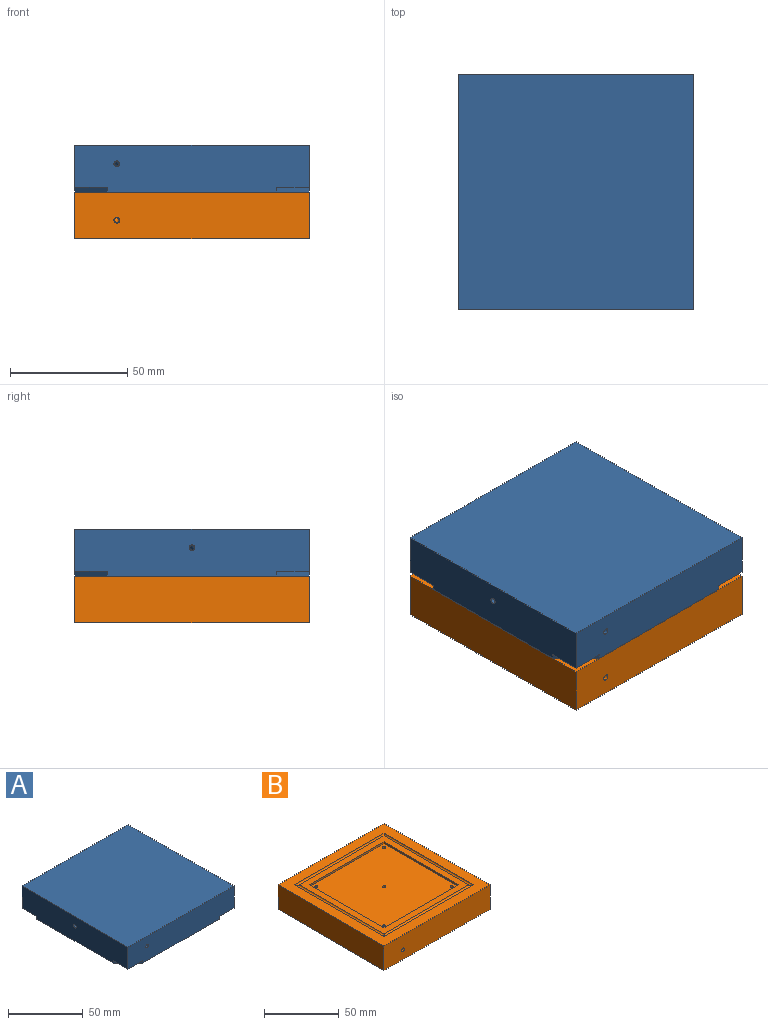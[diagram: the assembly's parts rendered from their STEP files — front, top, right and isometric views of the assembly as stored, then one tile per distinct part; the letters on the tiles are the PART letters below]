
ASSEMBLY  parts=2 mates=1
PART A: 49 faces, bbox 100x100x20 mm
  f0: cylinder r=1mm len=10.75mm, axis (0,1,0), area 67.5mm2, adj f35,f47
  f1: cylinder r=1mm len=8.75mm, axis (1,0,0), area 55mm2, adj f14,f45
  f2: cylinder r=1mm len=10.75mm, axis (0,-1,0), area 67.5mm2, adj f33,f43
  f3: cylinder r=1mm len=41.75mm, axis (-1,0,0), area 262.3mm2, adj f15,f41
  f4: cylinder r=1mm len=10.75mm, axis (-1,0,0), area 67.5mm2, adj f31,f39
  f5: cylinder r=1mm len=10.75mm, axis (-1,0,0), area 67.5mm2, adj f29,f37
  f6: plane 100x100mm, normal (0,0,-1), area 4708mm2, adj f9,f10,f11,f12,f16,f18,f20,f22
  f7: cylinder r=1mm len=5.5mm, axis (0,0,-1), area 34.6mm2, adj f14,f24
  f8: cylinder r=1mm len=5.5mm, axis (0,0,-1), area 34.6mm2, adj f15,f24
  f9: plane 100x20mm, normal (0,1,0), area 1939.1mm2, adj f6,f10,f11,f13,f20,f21,f22,f23
  f10: plane 100x20mm, normal (-1,0,0), area 1939.1mm2, adj f6,f9,f12,f13,f16,f17,f22,f23
  f11: plane 100x20mm, normal (1,0,0), area 1929.3mm2, adj f6,f9,f12,f13,f18,f19,f20,f21
  f12: plane 100x20mm, normal (0,-1,0), area 1939.1mm2, adj f6,f10,f11,f13,f16,f17,f18,f19
  f13: plane 100x100mm, normal (0,0,1), area 10000mm2, adj f9,f10,f11,f12
  f14: torus R=5mm, axis (0,1,0), area 49.3mm2, adj f1,f7
  f15: torus R=5mm, axis (0,-1,0), area 49.3mm2, adj f3,f8
  f16: plane 14x14mm, normal (-0.71,-0.71,0), area 39.6mm2, adj f6,f10,f12,f17
  f17: plane 14x14mm, normal (0,0,-1), area 98mm2, adj f10,f12,f16
  f18: plane 14x14mm, normal (0.71,-0.71,0), area 39.6mm2, adj f6,f11,f12,f19
  f19: plane 14x14mm, normal (0,0,-1), area 98mm2, adj f11,f12,f18
  f20: plane 14x14mm, normal (0.71,0.71,0), area 39.6mm2, adj f6,f9,f11,f21
  f21: plane 14x14mm, normal (0,0,-1), area 98mm2, adj f9,f11,f20
  f22: plane 14x14mm, normal (-0.71,0.71,0), area 39.6mm2, adj f6,f9,f10,f23
  f23: plane 14x14mm, normal (0,0,-1), area 98mm2, adj f9,f10,f22
  f24: plane 70x70mm, normal (0,0,-1), area 4881.2mm2, adj f7,f8,f25,f26,f27,f28,f30,f32
  f25: plane 70x1.5mm, normal (0,-1,0), area 105mm2, adj f6,f24,f26,f28
  f26: plane 70x1.5mm, normal (-1,0,0), area 105mm2, adj f6,f24,f25,f27
  f27: plane 70x1.5mm, normal (0,1,0), area 105mm2, adj f6,f24,f26,f28
  f28: plane 70x1.5mm, normal (1,0,0), area 105mm2, adj f6,f24,f25,f27
  f29: torus R=4mm, axis (0,-1,0), area 39.5mm2, adj f5,f30
  f30: cylinder r=1mm len=6.5mm, axis (0,0,-1), area 40.8mm2, adj f24,f29
  f31: torus R=4mm, axis (0,-1,0), area 39.5mm2, adj f4,f32
  f32: cylinder r=1mm len=6.5mm, axis (0,0,-1), area 40.8mm2, adj f24,f31
  f33: torus R=4mm, axis (1,0,0), area 39.5mm2, adj f2,f34
  f34: cylinder r=1mm len=6.5mm, axis (0,0,-1), area 40.8mm2, adj f24,f33
  f35: torus R=4mm, axis (-1,0,0), area 39.5mm2, adj f0,f36
  f36: cylinder r=1mm len=6.5mm, axis (0,0,-1), area 40.8mm2, adj f24,f35
  f37: cone r=0mm half-angle=59deg, axis (1,0,0), area 2.1mm2, adj f5,f38
  f38: cylinder r=1.25mm len=3.1mm, axis (1,0,0), area 24.3mm2, adj f11,f37
  f39: cone r=0mm half-angle=59deg, axis (1,0,0), area 2.1mm2, adj f4,f40
  f40: cylinder r=1.25mm len=3.1mm, axis (1,0,0), area 24.3mm2, adj f11,f39
  f41: cone r=0mm half-angle=59deg, axis (1,0,0), area 2.1mm2, adj f3,f42
  f42: cylinder r=1.25mm len=3.1mm, axis (1,0,0), area 24.3mm2, adj f11,f41
  f43: cone r=0mm half-angle=59deg, axis (0,1,0), area 2.1mm2, adj f2,f44
  f44: cylinder r=1.25mm len=3.1mm, axis (0,1,0), area 24.3mm2, adj f9,f43
  f45: cone r=0mm half-angle=59deg, axis (-1,0,0), area 2.1mm2, adj f1,f46
  f46: cylinder r=1.25mm len=3.1mm, axis (-1,0,0), area 24.3mm2, adj f10,f45
  f47: cone r=0mm half-angle=59deg, axis (0,-1,0), area 2.1mm2, adj f0,f48
  f48: cylinder r=1.25mm len=3.1mm, axis (0,-1,0), area 24.3mm2, adj f12,f47
PART B: 78 faces, bbox 100x100x20 mm
  f0: cylinder r=1mm len=10.75mm, axis (0,-1,0), area 67.5mm2, adj f60,f76
  f1: cylinder r=1mm len=10.75mm, axis (0,1,0), area 67.5mm2, adj f62,f74
  f2: cylinder r=1mm len=70.75mm, axis (1,0,0), area 444.5mm2, adj f23,f72
  f3: cylinder r=1mm len=82.75mm, axis (-1,0,0), area 519.9mm2, adj f31,f70
  f4: cylinder r=1mm len=10.75mm, axis (-1,0,0), area 67.5mm2, adj f56,f68
  f5: cylinder r=1mm len=41.75mm, axis (-1,0,0), area 262.3mm2, adj f54,f66
  f6: cylinder r=1mm len=10.75mm, axis (-1,0,0), area 67.5mm2, adj f58,f64
  f7: plane 100x100mm, normal (0,0,1), area 2944mm2, adj f8,f9,f10,f11,f50,f51,f52,f53
  f8: plane 100x20mm, normal (1,0,0), area 1975.5mm2, adj f7,f9,f10,f12,f65,f67,f69,f71
  f9: plane 100x20mm, normal (0,-1,0), area 1995.1mm2, adj f7,f8,f11,f12,f75
  f10: plane 100x20mm, normal (0,1,0), area 1995.1mm2, adj f7,f8,f11,f12,f77
  f11: plane 100x20mm, normal (-1,0,0), area 2000mm2, adj f7,f9,f10,f12
  f12: plane 100x100mm, normal (0,0,-1), area 10000mm2, adj f8,f9,f10,f11
  f13: torus R=4mm, axis (0,0,-1), area 39.5mm2, adj f14,f24
  f14: cylinder r=1mm len=14mm, axis (0,1,0), area 88mm2, adj f13,f15
  f15: torus R=4mm, axis (0,0,-1), area 39.5mm2, adj f14,f16
  f16: cylinder r=1mm len=28mm, axis (1,0,0), area 175.9mm2, adj f15,f17
  f17: torus R=4mm, axis (0,0,-1), area 39.5mm2, adj f16,f18
  f18: cylinder r=1mm len=32mm, axis (0,-1,0), area 201.1mm2, adj f17,f19
  f19: torus R=4mm, axis (0,0,-1), area 39.5mm2, adj f18,f20
  f20: cylinder r=1mm len=48mm, axis (-1,0,0), area 301.6mm2, adj f19,f21
  f21: torus R=4mm, axis (0,0,-1), area 39.5mm2, adj f20,f22
  f22: cylinder r=1mm len=50mm, axis (0,1,0), area 314.2mm2, adj f21,f23
  f23: torus R=4mm, axis (0,0,-1), area 39.5mm2, adj f2,f22
  f24: cylinder r=1mm len=10mm, axis (-1,0,0), area 62.4mm2, adj f13,f30
  f25: torus R=4mm, axis (0,0,1), area 39.5mm2, adj f26,f29
  f26: cylinder r=1mm len=2mm, axis (-1,0,0), area 12.6mm2, adj f25,f27
  f27: torus R=4mm, axis (0,0,1), area 39.5mm2, adj f26,f28
  f28: cylinder r=1mm len=5.54mm, axis (0,-1,0), area 34.8mm2, adj f27,f30
  f29: cylinder r=1mm len=13.66mm, axis (0,1,0), area 85.8mm2, adj f25,f43
  f30: bspline ~4.4x4mm, area 25.9mm2, adj f24,f28
  f31: torus R=4mm, axis (0,0,1), area 39.5mm2, adj f3,f32
  f32: cylinder r=1mm len=73mm, axis (0,-1,0), area 458.7mm2, adj f31,f33
  f33: torus R=4mm, axis (0,0,1), area 39.5mm2, adj f32,f34
  f34: cylinder r=1mm len=72mm, axis (1,0,0), area 452.4mm2, adj f33,f35
  f35: torus R=4mm, axis (0,0,1), area 39.5mm2, adj f34,f36
  f36: cylinder r=1mm len=50mm, axis (0,1,0), area 314.2mm2, adj f35,f37
  f37: torus R=4mm, axis (0,0,1), area 39.5mm2, adj f36,f38
  f38: cylinder r=1mm len=50mm, axis (-1,0,0), area 314.2mm2, adj f37,f39
  f39: torus R=4mm, axis (0,0,1), area 39.5mm2, adj f38,f40
  f40: cylinder r=1mm len=32mm, axis (0,-1,0), area 201.1mm2, adj f39,f41
  f41: torus R=4mm, axis (0,0,1), area 39.5mm2, adj f40,f42
  f42: cylinder r=1mm len=28mm, axis (1,0,0), area 175.9mm2, adj f41,f43
  f43: bspline ~5.34x5mm, area 41.4mm2, adj f29,f42
  f44: plane 70x70mm, normal (0,0,1), area 4884.3mm2, adj f45,f46,f47,f48,f55,f57,f59,f61
  f45: plane 70x1.5mm, normal (0,-1,0), area 105mm2, adj f44,f46,f48,f49
  f46: plane 70x1.5mm, normal (1,0,0), area 105mm2, adj f44,f45,f47,f49
  f47: plane 70x1.5mm, normal (0,1,0), area 105mm2, adj f44,f46,f48,f49
  f48: plane 70x1.5mm, normal (-1,0,0), area 105mm2, adj f44,f45,f47,f49
  f49: plane 80x80mm, normal (0,0,1), area 1500mm2, adj f45,f46,f47,f48,f50,f51,f52,f53
  f50: cylinder r=1mm len=84mm, axis (-1,0,0), area 257.6mm2, adj f7,f49,f51,f52
  f51: cylinder r=1mm len=84mm, axis (0,1,0), area 257.6mm2, adj f7,f49,f50,f53
  f52: cylinder r=1mm len=84mm, axis (0,-1,0), area 257.6mm2, adj f7,f49,f50,f53
  f53: cylinder r=1mm len=84mm, axis (1,0,0), area 257.6mm2, adj f7,f49,f51,f52
  f54: torus R=5mm, axis (0,1,0), area 49.3mm2, adj f5,f55
  f55: cylinder r=1mm len=5.5mm, axis (0,0,1), area 34.6mm2, adj f44,f54
  f56: torus R=4mm, axis (0,1,0), area 39.5mm2, adj f4,f57
  f57: cylinder r=1mm len=6.5mm, axis (0,0,1), area 40.8mm2, adj f44,f56
  f58: torus R=4mm, axis (0,1,0), area 39.5mm2, adj f6,f59
  f59: cylinder r=1mm len=6.5mm, axis (0,0,1), area 40.8mm2, adj f44,f58
  f60: torus R=4mm, axis (-1,0,0), area 39.5mm2, adj f0,f61
  f61: cylinder r=1mm len=6.5mm, axis (0,0,1), area 40.8mm2, adj f44,f60
  f62: torus R=4mm, axis (1,0,0), area 39.5mm2, adj f1,f63
  f63: cylinder r=1mm len=6.5mm, axis (0,0,1), area 40.8mm2, adj f44,f62
  f64: cone r=0mm half-angle=59deg, axis (1,0,0), area 2.1mm2, adj f6,f65
  f65: cylinder r=1.25mm len=3.1mm, axis (1,0,0), area 24.3mm2, adj f8,f64
  f66: cone r=0mm half-angle=59deg, axis (1,0,0), area 2.1mm2, adj f5,f67
  f67: cylinder r=1.25mm len=3.1mm, axis (1,0,0), area 24.3mm2, adj f8,f66
  f68: cone r=0mm half-angle=59deg, axis (1,0,0), area 2.1mm2, adj f4,f69
  f69: cylinder r=1.25mm len=3.1mm, axis (1,0,0), area 24.3mm2, adj f8,f68
  f70: cone r=0mm half-angle=59deg, axis (1,0,0), area 2.1mm2, adj f3,f71
  f71: cylinder r=1.25mm len=3.1mm, axis (1,0,0), area 24.3mm2, adj f8,f70
  f72: cone r=0mm half-angle=59deg, axis (1,0,0), area 2.1mm2, adj f2,f73
  f73: cylinder r=1.25mm len=3.1mm, axis (1,0,0), area 24.3mm2, adj f8,f72
  f74: cone r=0mm half-angle=59deg, axis (0,-1,0), area 2.1mm2, adj f1,f75
  f75: cylinder r=1.25mm len=3.1mm, axis (0,-1,0), area 24.3mm2, adj f9,f74
  f76: cone r=0mm half-angle=59deg, axis (0,1,0), area 2.1mm2, adj f0,f77
  f77: cylinder r=1.25mm len=3.1mm, axis (0,1,0), area 24.3mm2, adj f10,f76
PLACE A t=(-18.96,58.63,36.88)mm
PLACE B t=(-18.96,58.63,26.88)mm
MATE fastened B.f7 <-> A.f6  axis (0,0,1) through (-68.96,58.63,26.88)mm
